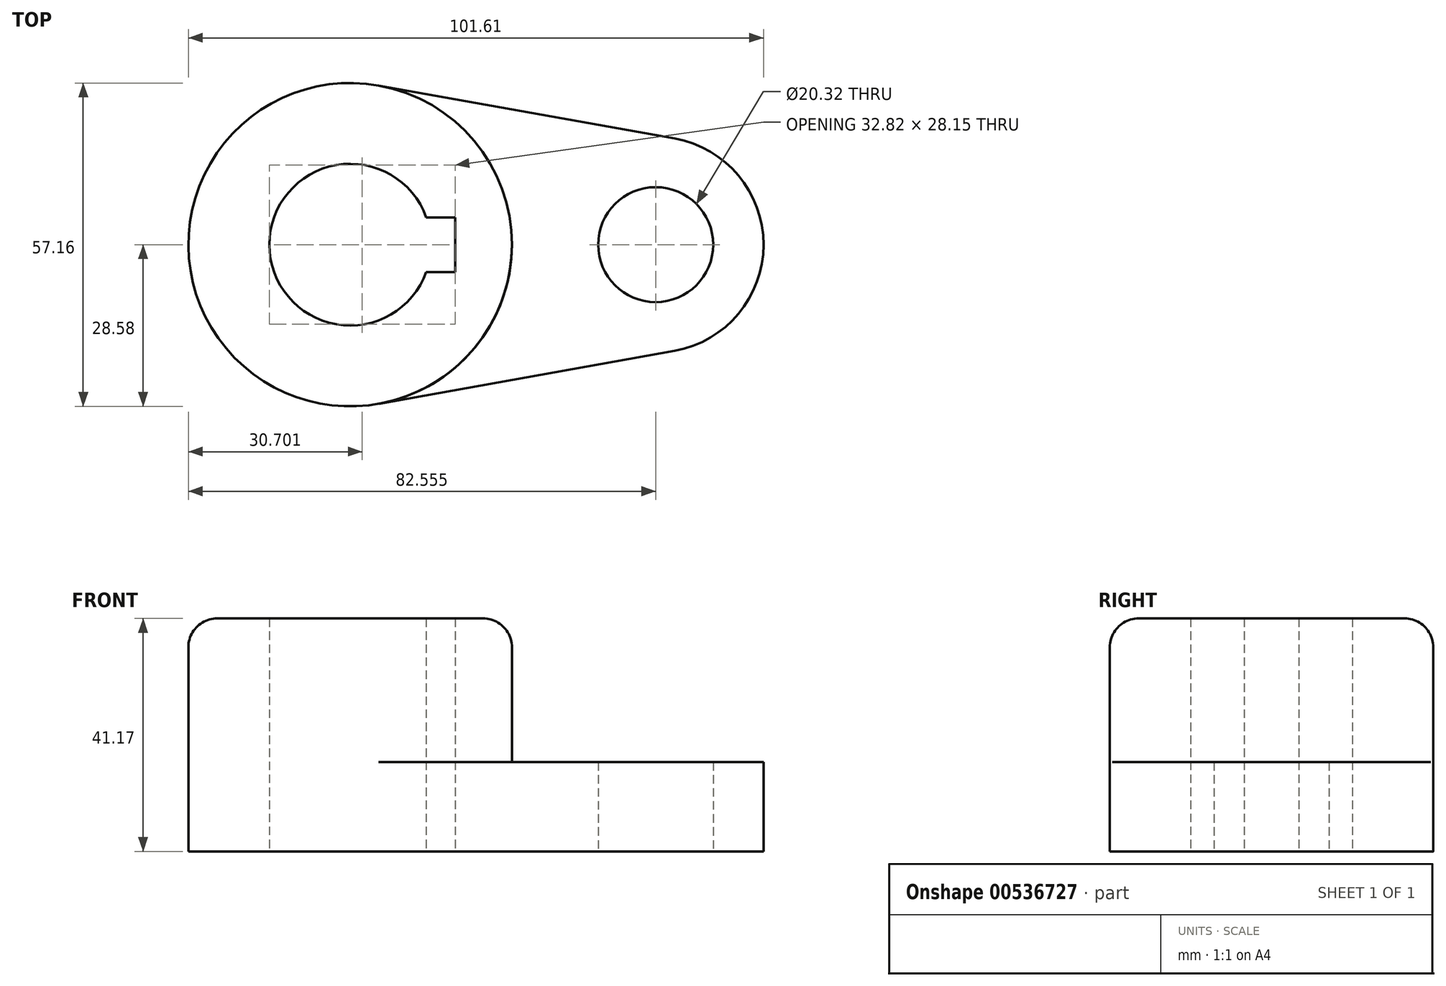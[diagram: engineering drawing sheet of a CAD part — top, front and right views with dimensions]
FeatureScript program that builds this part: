
annotation { "Feature Type Name" : "Feature", "Feature Type Description" : "" }
export const myFeature = defineFeature(function(context is Context, id is Id, definition is map)
    precondition{}
    {
        {
            var Q0;
            Q0=qCreatedBy(makeId("Top.planeOp"),FACE);
            var sketch = newSketch(context, id + "F0", { "sketchPlane" : qUnion([Q0])});
            skCircle(sketch, "E0", {"center": v(0, 0) * mm, "radius": 28.58 * mm});
            skArc(sketch, "E1", {"start": v(57.34, -18.75) * mm, "mid": v(73.03, 0) * mm, "end": v(57.34, 18.75) * mm});
            skLineSegment(sketch, "E2", {"start": v(5.04, 28.13) * mm, "end": v(57.34, 18.75) * mm});
            skLineSegment(sketch, "E3", {"start": v(5.04, -28.13) * mm, "end": v(57.34, -18.75) * mm});
            skCircle(sketch, "E4", {"center": v(53.98, 0) * mm, "radius": 10.16 * mm});
            skArc(sketch, "E5", {"start": v(13.45, 4.83) * mm, "mid": v(-14.29, 0) * mm, "end": v(13.45, -4.83) * mm});
            skLineSegment(sketch, "E6.bottom", {"start": v(18.53, 4.83) * mm, "end": v(13.45, 4.83) * mm});
            skLineSegment(sketch, "E6.top", {"start": v(18.53, -4.83) * mm, "end": v(13.45, -4.83) * mm});
            skLineSegment(sketch, "E6.left", {"start": v(18.53, 4.83) * mm, "end": v(18.53, -4.83) * mm});
            skPoint(sketch, "E6.middle", {"position": v(14.29, 0) * mm});
            skPoint(sketch, "E7.orphan", {"position": v(10.05, -4.83) * mm});
            skPoint(sketch, "E8.orphan", {"position": v(10.05, 4.83) * mm});
            skPoint(sketch, "E9", {"position": v(-14.29, 0) * mm});
            skSolve(sketch);
        }
        {
            var Q0;
            Q0 = qSketchRegion(id + "F0", true);
            extrude(context, id + "F1", {"entities" : qUnion([Q0]), "depth" : 15.77 * mm, "offsetDistance" : 25.4 * mm});
        }
        {
            var Q0;
            Q0=makeQuery(id+"F1.opExtrude","CAP_FACE",FACE,{"disambiguationData":[OSD([sQuery(id+"F0.wireOp",EDGE,"E0"),sQuery(id+"F0.wireOp",EDGE,"E1"),sQuery(id+"F0.wireOp",EDGE,"E2"),sQuery(id+"F0.wireOp",EDGE,"E3"),sQuery(id+"F0.wireOp",EDGE,"E4"),sQuery(id+"F0.wireOp",EDGE,"E5"),sQuery(id+"F0.wireOp",EDGE,"E6.bottom"),sQuery(id+"F0.wireOp",EDGE,"E6.top"),sQuery(id+"F0.wireOp",EDGE,"E6.left")])],"isStart":false});
            var sketch = newSketch(context, id + "F2", { "sketchPlane" : qUnion([Q0])});
            skCircle(sketch, "E10", {"center": v(0, 0) * mm, "radius": 28.58 * mm});
            skSolve(sketch);
        }
        {
            var Q0;
            Q0=makeQuery(id+"F2.imprint","IMPRINT",FACE,{"disambiguationData":[TD([[makeQuery(id+"F2.imprint","IMPRINT",EDGE,{"derivedFrom":makeQuery(id+"F1.opExtrude","CAP_EDGE",EDGE,{"disambiguationData":[OSD([sQuery(id+"F0.wireOp",EDGE,"E5")])],"isStart":false})}),-1.0]])]});
            extrude(context, id + "F3", {"entities" : qUnion([Q0]), "operationType" : NewBodyOperationType.ADD, "depth" : 25.4 * mm, "offsetDistance" : 25.4 * mm});
        }
        {
            var Q0;
            Q0=makeQuery(id+"F3.opExtrude","CAP_EDGE",EDGE,{"disambiguationData":[OSD([sQuery(id+"F2.wireOp",EDGE,"E10")])],"isStart":false});
            fillet(context, id + "F4", {"entities" : qUnion([Q0]), "radius" : 5.08 * mm, "tangentPropagation" : true, "allowEdgeOverflow" : false});
        }
    });
